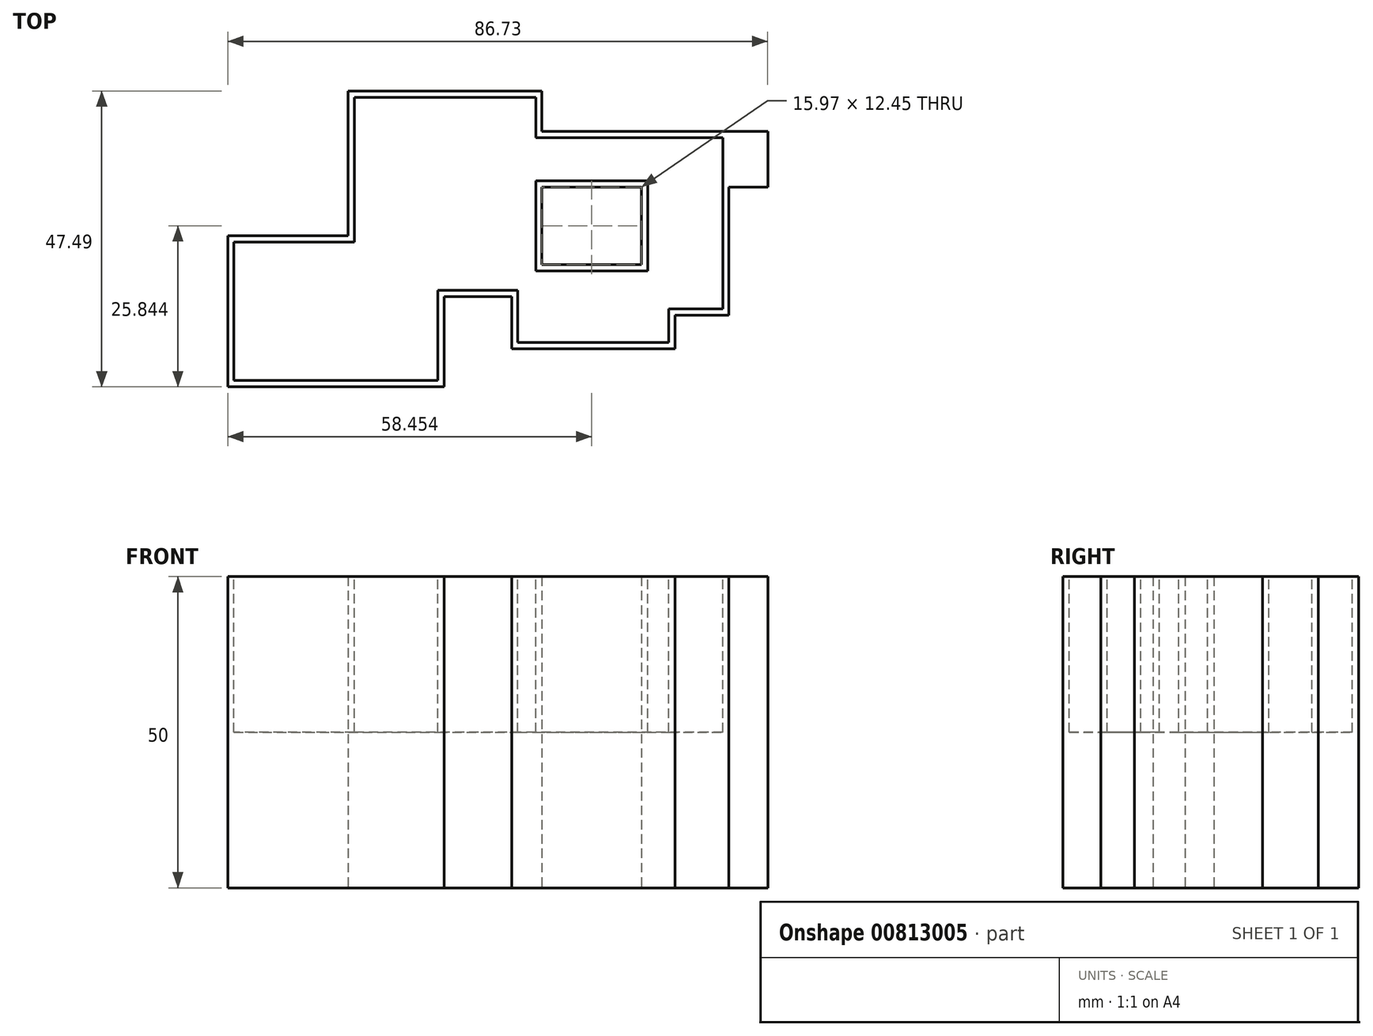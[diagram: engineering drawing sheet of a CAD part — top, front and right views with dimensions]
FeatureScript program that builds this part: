
annotation { "Feature Type Name" : "Feature", "Feature Type Description" : "" }
export const myFeature = defineFeature(function(context is Context, id is Id, definition is map)
    precondition{}
    {
        {
            var Q0;
            Q0=qCreatedBy(makeId("Top.planeOp"),FACE);
            var sketch = newSketch(context, id + "F0", { "sketchPlane" : qUnion([Q0])});
            skLineSegment(sketch, "E0.bottom", {"start": v(0, 0) * mm, "end": v(34.77, 0) * mm});
            skLineSegment(sketch, "E0.top", {"start": v(0, 24.22) * mm, "end": v(34.77, 24.22) * mm});
            skLineSegment(sketch, "E0.left", {"start": v(0, 0) * mm, "end": v(0, 24.22) * mm});
            skLineSegment(sketch, "E0.right", {"start": v(34.77, 0) * mm, "end": v(34.77, 24.22) * mm});
            skLineSegment(sketch, "E1.bottom", {"start": v(19.35, 14.48) * mm, "end": v(50.47, 14.48) * mm});
            skLineSegment(sketch, "E1.top", {"start": v(19.35, 47.5) * mm, "end": v(50.47, 47.5) * mm});
            skLineSegment(sketch, "E1.left", {"start": v(19.35, 14.48) * mm, "end": v(19.35, 47.5) * mm});
            skLineSegment(sketch, "E1.right", {"start": v(50.47, 14.48) * mm, "end": v(50.47, 47.5) * mm});
            skLineSegment(sketch, "E2.bottom", {"start": v(45.6, 19.62) * mm, "end": v(71.85, 19.62) * mm});
            skLineSegment(sketch, "E2.top", {"start": v(45.6, 6.09) * mm, "end": v(71.85, 6.09) * mm});
            skLineSegment(sketch, "E2.left", {"start": v(45.6, 19.62) * mm, "end": v(45.6, 6.09) * mm});
            skLineSegment(sketch, "E2.right", {"start": v(71.85, 19.62) * mm, "end": v(71.85, 6.09) * mm});
            skLineSegment(sketch, "E3.bottom", {"start": v(45.33, 41) * mm, "end": v(86.73, 41) * mm});
            skLineSegment(sketch, "E3.top", {"start": v(45.33, 32.07) * mm, "end": v(86.73, 32.07) * mm});
            skLineSegment(sketch, "E3.left", {"start": v(45.33, 41) * mm, "end": v(45.33, 32.07) * mm});
            skLineSegment(sketch, "E3.right", {"start": v(86.73, 41) * mm, "end": v(86.73, 32.07) * mm});
            skLineSegment(sketch, "E4.bottom", {"start": v(66.44, 36.67) * mm, "end": v(80.5, 36.67) * mm});
            skLineSegment(sketch, "E4.top", {"start": v(66.44, 11.5) * mm, "end": v(80.5, 11.5) * mm});
            skLineSegment(sketch, "E4.left", {"start": v(66.44, 36.67) * mm, "end": v(66.44, 11.5) * mm});
            skLineSegment(sketch, "E4.right", {"start": v(80.5, 36.67) * mm, "end": v(80.5, 11.5) * mm});
            skSolve(sketch);
        }
        {
            var Q0;
            {var subQ1=sQuery(id+"F0.wireOp",EDGE,"E0.bottom");Q0=makeQuery(id+"F0.imprint","IMPRINT",FACE,{"disambiguationData":[TD([[makeQuery(id+"F0.imprint","IMPRINT",EDGE,{"derivedFrom":subQ1}),1.0]])]});}
            var Q1;
            {var subQ1=sQuery(id+"F0.wireOp",EDGE,"E1.top");Q1=makeQuery(id+"F0.imprint","IMPRINT",FACE,{"disambiguationData":[TD([[makeQuery(id+"F0.imprint","IMPRINT",EDGE,{"derivedFrom":subQ1}),-1.0]])]});}
            var Q2;
            {var subQ0=sQuery(id+"F0.wireOp",EDGE,"E2.top");Q2=makeQuery(id+"F0.imprint","IMPRINT",FACE,{"disambiguationData":[TD([[makeQuery(id+"F0.imprint","IMPRINT",EDGE,{"derivedFrom":subQ0}),1.0]])]});}
            var Q3;
            {var subQ3=sQuery(id+"F0.wireOp",EDGE,"E2.right");var subQ5=sQuery(id+"F0.wireOp",EDGE,"E2.bottom");var subQ6=makeQuery(id+"F0.imprint","INTERSECT",VERTEX,{"derivedFrom":[subQ5,subQ3]});Q3=makeQuery(id+"F0.imprint","IMPRINT",FACE,{"disambiguationData":[TD([[makeQuery(id+"F0.imprint","IMPRINT",EDGE,{"disambiguationData":[TD([[subQ6,1.0]])],"derivedFrom":subQ5}),1.0]])]});}
            var Q4;
            {var subQ8=sQuery(id+"F0.wireOp",EDGE,"E3.right");Q4=makeQuery(id+"F0.imprint","IMPRINT",FACE,{"disambiguationData":[TD([[makeQuery(id+"F0.imprint","IMPRINT",EDGE,{"derivedFrom":subQ8}),-1.0]])]});}
            var Q5;
            {var subQ5=sQuery(id+"F0.wireOp",EDGE,"E3.left");Q5=makeQuery(id+"F0.imprint","IMPRINT",FACE,{"disambiguationData":[TD([[makeQuery(id+"F0.imprint","IMPRINT",EDGE,{"derivedFrom":subQ5}),1.0]])]});}
            var Q6;
            {var subQ5=sQuery(id+"F0.wireOp",EDGE,"E4.bottom");Q6=makeQuery(id+"F0.imprint","IMPRINT",FACE,{"disambiguationData":[TD([[makeQuery(id+"F0.imprint","IMPRINT",EDGE,{"derivedFrom":subQ5}),-1.0]])]});}
            var Q7;
            {var subQ0=sQuery(id+"F0.wireOp",EDGE,"E1.right");var subQ1=sQuery(id+"F0.wireOp",EDGE,"E1.bottom");var subQ2=makeQuery(id+"F0.imprint","INTERSECT",VERTEX,{"derivedFrom":[subQ1,subQ0]});Q7=makeQuery(id+"F0.imprint","IMPRINT",FACE,{"disambiguationData":[TD([[makeQuery(id+"F0.imprint","IMPRINT",EDGE,{"disambiguationData":[TD([[subQ2,1.0]])],"derivedFrom":subQ1}),1.0]])]});}
            var Q8;
            {var subQ0=sQuery(id+"F0.wireOp",EDGE,"E2.right");var subQ1=sQuery(id+"F0.wireOp",EDGE,"E2.bottom");var subQ2=makeQuery(id+"F0.imprint","INTERSECT",VERTEX,{"derivedFrom":[subQ1,subQ0]});Q8=makeQuery(id+"F0.imprint","IMPRINT",FACE,{"disambiguationData":[TD([[makeQuery(id+"F0.imprint","IMPRINT",EDGE,{"disambiguationData":[TD([[subQ2,1.0]])],"derivedFrom":subQ1}),-1.0]])]});}
            var Q9;
            {var subQ0=sQuery(id+"F0.wireOp",EDGE,"E0.right");var subQ1=sQuery(id+"F0.wireOp",EDGE,"E0.top");var subQ2=makeQuery(id+"F0.imprint","INTERSECT",VERTEX,{"derivedFrom":[subQ1,subQ0]});Q9=makeQuery(id+"F0.imprint","IMPRINT",FACE,{"disambiguationData":[TD([[makeQuery(id+"F0.imprint","IMPRINT",EDGE,{"disambiguationData":[TD([[subQ2,1.0]])],"derivedFrom":subQ1}),-1.0]])]});}
            extrude(context, id + "F1", {"entities" : qUnion([Q0, Q1, Q2, Q3, Q4, Q5, Q6, Q7, Q8, Q9]), "depth" : 50 * mm, "offsetDistance" : 25 * mm});
        }
        {
            var Q0;
            Q0=makeQuery(id+"F1.opExtrude","CAP_FACE",FACE,{"disambiguationData":[OSD([sQuery(id+"F0.wireOp",EDGE,"E0.bottom"),sQuery(id+"F0.wireOp",EDGE,"E0.top"),sQuery(id+"F0.wireOp",EDGE,"E0.left"),sQuery(id+"F0.wireOp",EDGE,"E0.right"),sQuery(id+"F0.wireOp",EDGE,"E1.bottom"),sQuery(id+"F0.wireOp",EDGE,"E1.top"),sQuery(id+"F0.wireOp",EDGE,"E1.left"),sQuery(id+"F0.wireOp",EDGE,"E1.right"),sQuery(id+"F0.wireOp",EDGE,"E2.bottom"),sQuery(id+"F0.wireOp",EDGE,"E2.top"),sQuery(id+"F0.wireOp",EDGE,"E2.left"),sQuery(id+"F0.wireOp",EDGE,"E2.right"),sQuery(id+"F0.wireOp",EDGE,"E3.bottom"),sQuery(id+"F0.wireOp",EDGE,"E3.top"),sQuery(id+"F0.wireOp",EDGE,"E3.right"),sQuery(id+"F0.wireOp",EDGE,"E4.top"),sQuery(id+"F0.wireOp",EDGE,"E4.left"),sQuery(id+"F0.wireOp",EDGE,"E4.right")])],"isStart":false});
            var sketch = newSketch(context, id + "F2", { "sketchPlane" : qUnion([Q0])});
            skLineSegment(sketch, "E5.0", {"start": v(1, 1) * mm, "end": v(33.77, 1) * mm});
            skLineSegment(sketch, "E5.1", {"start": v(1, 23.22) * mm, "end": v(1, 1) * mm});
            skLineSegment(sketch, "E5.2", {"start": v(20.35, 23.22) * mm, "end": v(1, 23.22) * mm});
            skLineSegment(sketch, "E5.3", {"start": v(70.85, 7.09) * mm, "end": v(70.85, 12.5) * mm});
            skLineSegment(sketch, "E5.4", {"start": v(46.6, 7.09) * mm, "end": v(70.85, 7.09) * mm});
            skLineSegment(sketch, "E5.5", {"start": v(46.6, 15.48) * mm, "end": v(46.6, 7.09) * mm});
            skLineSegment(sketch, "E5.6", {"start": v(33.77, 15.48) * mm, "end": v(46.6, 15.48) * mm});
            skLineSegment(sketch, "E5.7", {"start": v(70.85, 12.5) * mm, "end": v(79.5, 12.5) * mm});
            skLineSegment(sketch, "E5.8", {"start": v(79.5, 12.5) * mm, "end": v(79.5, 40) * mm});
            skLineSegment(sketch, "E5.9", {"start": v(79.5, 40) * mm, "end": v(49.47, 40) * mm});
            skLineSegment(sketch, "E5.10", {"start": v(33.77, 1) * mm, "end": v(33.77, 15.48) * mm});
            skLineSegment(sketch, "E5.11", {"start": v(49.47, 40) * mm, "end": v(49.47, 46.5) * mm});
            skLineSegment(sketch, "E5.12", {"start": v(49.47, 46.5) * mm, "end": v(20.35, 46.5) * mm});
            skLineSegment(sketch, "E5.13", {"start": v(20.35, 46.5) * mm, "end": v(20.35, 23.22) * mm});
            skLineSegment(sketch, "E6.0", {"start": v(49.47, 18.62) * mm, "end": v(49.47, 33.07) * mm});
            skLineSegment(sketch, "E6.1", {"start": v(49.47, 18.62) * mm, "end": v(67.44, 18.62) * mm});
            skLineSegment(sketch, "E6.2", {"start": v(67.44, 33.07) * mm, "end": v(67.44, 18.62) * mm});
            skLineSegment(sketch, "E6.3", {"start": v(49.47, 33.07) * mm, "end": v(67.44, 33.07) * mm});
            skSolve(sketch);
        }
        {
            var Q0;
            Q0=makeQuery(id+"F2.imprint","IMPRINT",FACE,{"disambiguationData":[TD([[makeQuery(id+"F2.imprint","IMPRINT",EDGE,{"derivedFrom":sQuery(id+"F2.wireOp",EDGE,"E5.0")}),1.0]])]});
            extrude(context, id + "F3", {"entities" : qUnion([Q0]), "operationType" : NewBodyOperationType.REMOVE, "oppositeDirection" : true, "depth" : 25 * mm, "offsetDistance" : 25 * mm});
        }
    });
